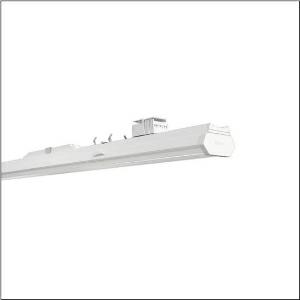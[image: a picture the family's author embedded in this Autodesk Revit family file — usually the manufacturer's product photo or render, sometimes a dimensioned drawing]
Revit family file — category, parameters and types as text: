
# Revit family: licross_r__11_protected_ho_51tp12dn4fxm_edee
name_source: partatom
category: Lighting Fixtures
units: mm (PartAtom-declared; Revit-internal decimal feet)

## family parameters
Cut with Voids When Loaded = No
Host = Face
Light Source = No
Part Type = Normal
Room Calculation Point = No
Round Connector Dimension = Use Diameter
Shared = No

## types (1)
- --- (1 x LED, 15270 lm, 87.3 W, 4000K)
    Apparent Load = 87 VA
    CIE Flux Codes = 70 91 97 98 100
    Color Rendering = 80
    Color Temperature = 4000K
    Default Elevation = 1800 mm
    Description = Licross® 11 Protected HO, luminaire insert, of sheet steel, galvanised, coil coated, white, length: 1.500mm, width: 90mm, height: 101mm, LED rated luminous flux: 15.270lm, light colour: 840, control gear: DALI 2, with plug, 5-pole, with phase selection, mains connection: 220..240V, AC, 50/60Hz, rated input power: 87W, internal wiring halogen-free, primary optical cover: cover, of PMMA, light emission: direct distribution, primary light characteristic: symmetric, protection rating (complete): IP64, insulation class (complete): insulation class I (protective earthing), certification: CE, ENEC, VDE, UKCA, protection symbol: D if used in an environment with conductive dust loads with corresponding accessories, impact resistance: IK06, permissible ambient temperature for indoor applications: -25..+30°C, corresponds to IFS (International Featured Standards) requirements for safety and quality in the food industry, reducing of maximum allowable ambient temperature of 5°C with ceiling mounting, LABS conformity tested according to VDMA 24364:2018-05, packaging unit: 1 piece
    Height = 92 mm
    Lamp = 1 x LED
    Lamp Light Flux = 15270 lm
    Lamp Power = 87.3 W
    Lamp count = 1
    Length = 1500 mm
    Luminous efficacy = 175 lm/W
    Manufacturer = Siteco
    ModVariant = No
    Model = 51TP12DN4FXM
    Mounting Place = Ceiling
    Mounting Type = Pendant
    Number of Poles = 1
    OnlyDefault = Yes
    Power Factor = 1
    Product Name = Licross® 11 Protected HO
    Product group = luminaire insert | ceiling pendant
    ProductGroupID = 902
    Protection Class = Protection class I
    Protection Degree = IP 64
    RLX_Detail_Level = 1
    RLX_Emergency_Light_Flux = 0 lm
    RLX_Emergency_Type = 0
    RLX_Emergency_Type_DB = No
    RlxData = <blob elided: 24461 chars, md5=77c7437a>
    Socket = socket
    Standby Power = 0 W
    System Light Flux = 15270 lm
    System Power = 87 W
    Type Comments = factory setting: luminous flux: 100 % | dim-lin: 254 | 589 mA
    Type Image = l_1256148.jpg
    URL = http://relux.com
    VarID = @adj_030601
    Voltage = 0 V
    Weight = 0.00 kg
    Width = 88 mm

## geometry (parser evidence)
native form markers: Blend x4, Sweep x9
no freeform markers — native parametric forms only
